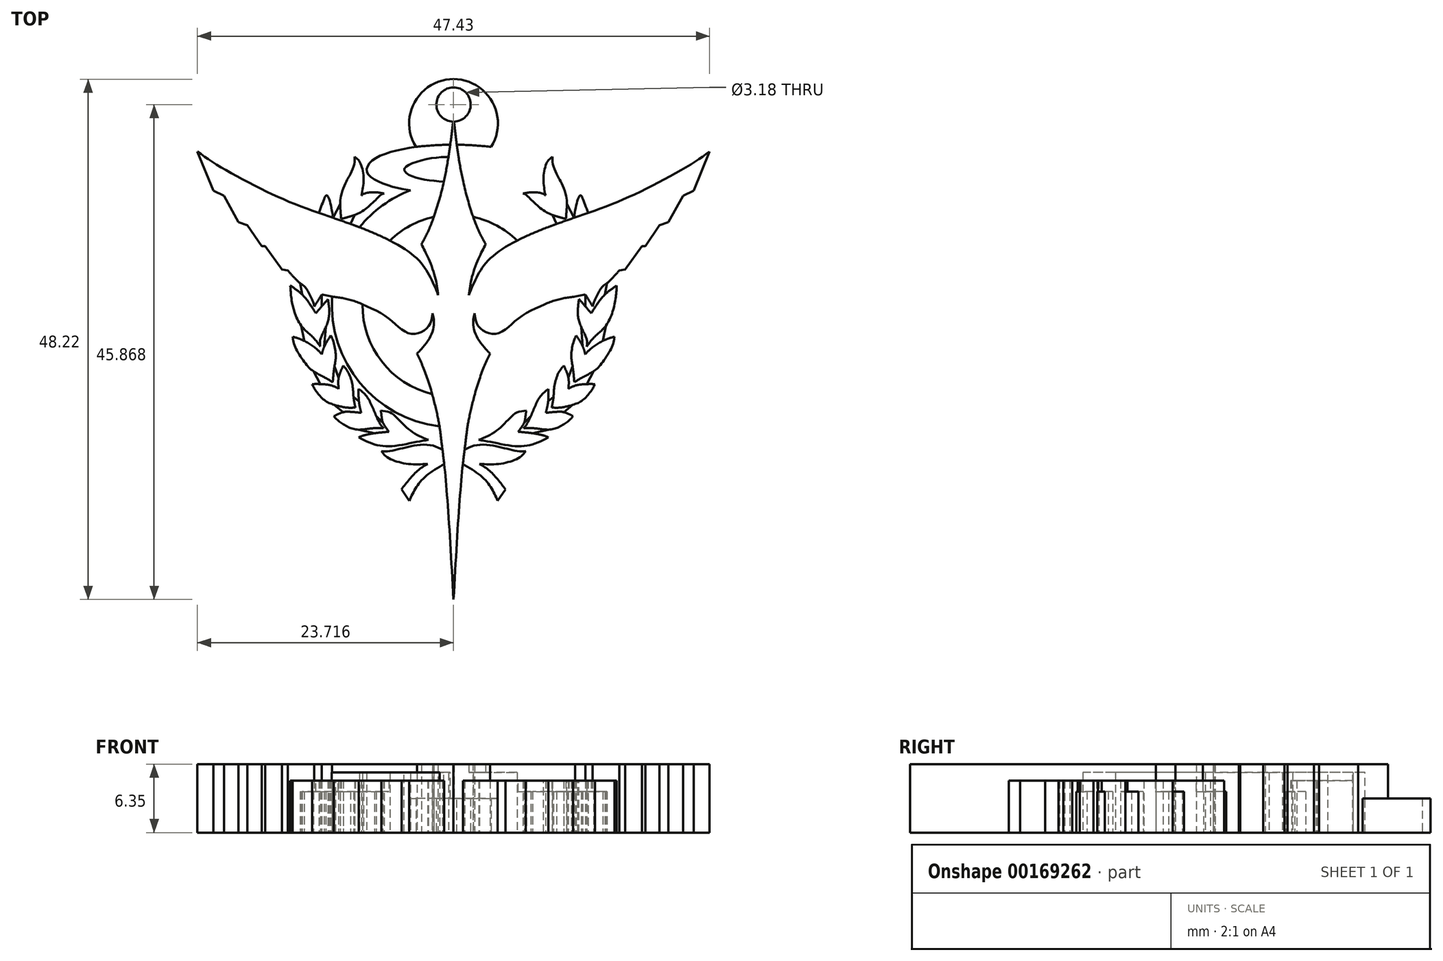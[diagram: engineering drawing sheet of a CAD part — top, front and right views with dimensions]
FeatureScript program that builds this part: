
annotation { "Feature Type Name" : "Feature", "Feature Type Description" : "" }
export const myFeature = defineFeature(function(context is Context, id is Id, definition is map)
    precondition{}
    {
        {
            var Q0;
            Q0=qCreatedBy(makeId("Top.planeOp"),FACE);
            var sketch = newSketch(context, id + "F0", { "sketchPlane" : qUnion([Q0])});
            skFitSpline(sketch, "E0", {"points": [v(-0.2, 21.86) * mm, v(-1.04, 16.18) * mm, v(-2.36, 11.79) * mm, v(-3.17, 10.17) * mm], "startDerivative": vector(-1.64, -14.05) * mm, "endDerivative": vector(-3.45, -6.14) * mm});
            skFitSpline(sketch, "E1", {"points": [v(-3.17, 10.17) * mm, v(-2.63, 9.12) * mm, v(-1.89, 7.1) * mm, v(-1.62, 5.47) * mm], "startDerivative": vector(1.83, -3.3) * mm, "endDerivative": vector(0.52, -4.63) * mm});
            skFitSpline(sketch, "E2", {"points": [v(-1.62, 5.47) * mm, v(-2.4, 7.23) * mm, v(-3.85, 9.08) * mm, v(-8.07, 11.42) * mm, v(-13.34, 13.3) * mm, v(-17.53, 15.06) * mm, v(-21.76, 17.33) * mm, v(-23.91, 18.75) * mm], "startDerivative": vector(-6.88, 17.13) * mm, "endDerivative": vector(-16.15, 11.23) * mm});
            skLineSegment(sketch, "E3", {"start": v(-23.91, 18.75) * mm, "end": v(-22.43, 15.13) * mm});
            skLineSegment(sketch, "E4", {"start": v(-22.43, 15.13) * mm, "end": v(-21.45, 14.66) * mm});
            skLineSegment(sketch, "E5", {"start": v(-21.45, 14.66) * mm, "end": v(-20.1, 12.23) * mm});
            skLineSegment(sketch, "E6", {"start": v(-20.1, 12.23) * mm, "end": v(-19.28, 11.93) * mm});
            skLineSegment(sketch, "E7", {"start": v(-19.28, 11.93) * mm, "end": v(-17.97, 9.98) * mm});
            skLineSegment(sketch, "E8", {"start": v(-17.97, 9.98) * mm, "end": v(-17.65, 9.98) * mm});
            skLineSegment(sketch, "E9", {"start": v(-17.65, 9.98) * mm, "end": v(-16.08, 7.83) * mm});
            skLineSegment(sketch, "E10", {"start": v(-16.08, 7.83) * mm, "end": v(-15.53, 7.73) * mm});
            skFitSpline(sketch, "E11", {"points": [v(-15.53, 7.73) * mm, v(-15.08, 7.22) * mm, v(-14.4, 6.55) * mm, v(-13.97, 6.24) * mm, v(-13.58, 5.63) * mm, v(-13.19, 4.78) * mm, v(-13.09, 4.4) * mm], "startDerivative": vector(2.54, -2.85) * mm, "endDerivative": vector(0.52, -2.73) * mm});
            skFitSpline(sketch, "E12", {"points": [v(-13.09, 4.4) * mm, v(-12.8, 4.88) * mm, v(-12.4, 5.52) * mm], "startDerivative": vector(0.58, 1.01) * mm, "endDerivative": vector(0.8, 1.23) * mm});
            skFitSpline(sketch, "E13", {"points": [v(-12.4, 5.52) * mm, v(-11.44, 5.32) * mm], "startDerivative": vector(0.95, -0.2) * mm, "endDerivative": vector(0.95, -0.2) * mm});
            skArc(sketch, "E14", {"start": v(-4.19, 15.16) * mm, "mid": v(-6.77, 13.76) * mm, "end": v(-8.9, 11.74) * mm});
            skFitSpline(sketch, "E15", {"points": [v(-0.5, 19.4) * mm, v(-3.68, 19.19) * mm, v(-6.74, 18.47) * mm, v(-8.03, 17.61) * mm, v(-8.22, 16.9) * mm, v(-7.62, 16.23) * mm, v(-5.78, 15.49) * mm, v(-4.19, 15.16) * mm], "startDerivative": vector(-16.33, -0.58) * mm, "endDerivative": vector(11.13, -1.82) * mm});
            skFitSpline(sketch, "E16", {"points": [v(-0.66, 18.27) * mm, v(-0.92, 18.25) * mm, v(-2.56, 18.09) * mm, v(-4.33, 17.52) * mm, v(-4.77, 17.11) * mm, v(-4.38, 16.63) * mm, v(-2.99, 16.18) * mm, v(-1.1, 15.96) * mm], "startDerivative": vector(-3.86, -1.21) * mm, "endDerivative": vector(10.06, -0.87) * mm});
            skArc(sketch, "E17.trimOffspring", {"start": v(-11.44, 5.32) * mm, "mid": v(-8.86, -2.68) * mm, "end": v(-1.5, -6.72) * mm});
            skFitSpline(sketch, "E18", {"points": [v(-11.44, 5.32) * mm, v(-9.96, 5.07) * mm, v(-8.12, 4.38) * mm, v(-6.21, 3.3) * mm, v(-4.97, 2.25) * mm, v(-3.92, 1.85) * mm, v(-3.01, 2.13) * mm, v(-2.37, 2.78) * mm, v(-2.15, 3.78) * mm], "startDerivative": vector(11.12, -1.28) * mm, "endDerivative": vector(0.96, 9.95) * mm});
            skFitSpline(sketch, "E19", {"points": [v(-2.15, 3.78) * mm, v(-2.01, 3) * mm, v(-2.39, 1.5) * mm, v(-3.4, 0.2) * mm, v(-3.57, 0.03) * mm], "startDerivative": vector(0.85, -3.16) * mm, "endDerivative": vector(-0.96, -1.05) * mm});
            skFitSpline(sketch, "E20", {"points": [v(-3.57, 0.03) * mm, v(-3.03, -1.16) * mm, v(-2.36, -3.05) * mm, v(-1.77, -5.3) * mm, v(-1.5, -6.72) * mm, v(-1.32, -8.08) * mm, v(-1.09, -9.94) * mm, v(-0.73, -14) * mm, v(-0.2, -22.75) * mm], "startDerivative": vector(5.95, -12.65) * mm, "endDerivative": vector(2.3, -40.95) * mm});
            skArc(sketch, "E21", {"start": v(-2.01, 12.71) * mm, "mid": v(-4.2, 11.9) * mm, "end": v(-6.08, 10.51) * mm});
            skArc(sketch, "E22.trimOffspring", {"start": v(-8.62, 4.6) * mm, "mid": v(-6.85, -0.69) * mm, "end": v(-2.17, -3.71) * mm});
            skFitSpline(sketch, "E23", {"points": [v(-9.37, 18.29) * mm, v(-9.4, 17.58) * mm, v(-9.87, 16.43) * mm, v(-10.1, 16.05) * mm, v(-10.6, 14.72) * mm, v(-10.7, 13.9) * mm, v(-10.6, 12.52) * mm], "startDerivative": vector(0.36, -4.44) * mm, "endDerivative": vector(0.6, -7.53) * mm});
            skFitSpline(sketch, "E24", {"points": [v(-10.6, 12.52) * mm, v(-9.35, 12.88) * mm, v(-8.4, 13.4) * mm, v(-7.35, 14.33) * mm, v(-6.81, 14.81) * mm, v(-6.63, 14.87) * mm], "startDerivative": vector(5.33, 1.36) * mm, "endDerivative": vector(1.78, 0.34) * mm});
            skFitSpline(sketch, "E25", {"points": [v(-6.63, 14.87) * mm, v(-7.46, 15) * mm, v(-8.44, 14.87) * mm, v(-8.7, 14.7) * mm], "startDerivative": vector(-2.08, 0.45) * mm, "endDerivative": vector(-0.93, -0.78) * mm});
            skFitSpline(sketch, "E26", {"points": [v(-8.7, 14.7) * mm, v(-8.53, 16.35) * mm, v(-8.89, 17.8) * mm, v(-9.37, 18.29) * mm], "startDerivative": vector(0.8, 4.17) * mm, "endDerivative": vector(-2.07, 1.52) * mm});
            skFitSpline(sketch, "E27", {"points": [v(-12.66, 13.07) * mm, v(-12.2, 14.33) * mm, v(-11.96, 14.7) * mm, v(-11.7, 14.33) * mm, v(-11.35, 12.62) * mm], "startDerivative": vector(1.61, 4.49) * mm, "endDerivative": vector(0.87, -5.57) * mm});
            skFitSpline(sketch, "E28", {"points": [v(-15.3, 6.34) * mm, v(-15.13, 4.67) * mm, v(-14.31, 2.64) * mm, v(-13.27, 1.61) * mm, v(-12.54, 0.7) * mm], "startDerivative": vector(0.31, -6.23) * mm, "endDerivative": vector(3.16, -4.45) * mm});
            skFitSpline(sketch, "E29", {"points": [v(-12.54, 0.7) * mm, v(-12.54, 1.33) * mm, v(-12.02, 2.49) * mm, v(-11.7, 3.7) * mm, v(-11.81, 5.08) * mm], "startDerivative": vector(-0.45, 3.14) * mm, "endDerivative": vector(-0.71, 5.07) * mm});
            skFitSpline(sketch, "E30", {"points": [v(-11.81, 5.08) * mm, v(-12.4, 4.43) * mm, v(-12.94, 3.77) * mm], "startDerivative": vector(-1.16, -1.28) * mm, "endDerivative": vector(-1.1, -1.33) * mm});
            skFitSpline(sketch, "E31", {"points": [v(-12.94, 3.77) * mm, v(-13.42, 4.52) * mm, v(-14.22, 5.52) * mm, v(-15.3, 6.34) * mm], "startDerivative": vector(-1.54, 2.48) * mm, "endDerivative": vector(-3.16, 2.11) * mm});
            skFitSpline(sketch, "E32", {"points": [v(-15.1, 1.6) * mm, v(-14.03, 1.22) * mm, v(-12.73, 0.33) * mm, v(-12.4, -0.03) * mm], "startDerivative": vector(2.86, -0.78) * mm, "endDerivative": vector(1.1, -1.39) * mm});
            skFitSpline(sketch, "E33", {"points": [v(-12.4, -0.03) * mm, v(-12.16, 0.7) * mm, v(-11.56, 1.72) * mm], "startDerivative": vector(0.38, 1.58) * mm, "endDerivative": vector(1.24, 1.9) * mm});
            skFitSpline(sketch, "E34", {"points": [v(-11.56, 1.72) * mm, v(-11.3, 1.1) * mm, v(-11.1, -0.23) * mm, v(-11.22, -1.13) * mm, v(-11.38, -2.62) * mm], "startDerivative": vector(1.38, -2.72) * mm, "endDerivative": vector(-0.47, -5.48) * mm});
            skFitSpline(sketch, "E35", {"points": [v(-11.38, -2.62) * mm, v(-12, -2.24) * mm, v(-13.17, -1.6) * mm, v(-13.9, -0.9) * mm, v(-14.88, 0.7) * mm, v(-15.1, 1.6) * mm], "startDerivative": vector(-3.43, 2.26) * mm, "endDerivative": vector(-0.6, 4.58) * mm});
            skFitSpline(sketch, "E36", {"points": [v(-10.4, -1.09) * mm, v(-9.92, -1.74) * mm, v(-9.54, -2.96) * mm, v(-9.45, -3.98) * mm, v(-9.28, -4.96) * mm], "startDerivative": vector(2.28, -2.57) * mm, "endDerivative": vector(0.84, -4) * mm});
            skFitSpline(sketch, "E37", {"points": [v(-9.28, -4.96) * mm, v(-10.07, -4.96) * mm, v(-11.24, -4.7) * mm, v(-12.12, -4.3) * mm, v(-12.9, -3.46) * mm, v(-13.29, -2.8) * mm], "startDerivative": vector(-4.07, -0.25) * mm, "endDerivative": vector(-1.83, 3.6) * mm});
            skFitSpline(sketch, "E38", {"points": [v(-13.29, -2.8) * mm, v(-12.54, -2.8) * mm, v(-11.49, -2.92) * mm, v(-10.83, -3.23) * mm], "startDerivative": vector(2.24, 0.04) * mm, "endDerivative": vector(1.91, -1.15) * mm});
            skFitSpline(sketch, "E39", {"points": [v(-10.83, -3.23) * mm, v(-10.83, -2.2) * mm, v(-10.4, -1.09) * mm], "startDerivative": vector(-0.2, 2.12) * mm, "endDerivative": vector(1.03, 2.17) * mm});
            skFitSpline(sketch, "E40", {"points": [v(-8.99, -3.23) * mm, v(-8.96, -4.4) * mm, v(-8.74, -5.45) * mm], "startDerivative": vector(-0.04, -2.32) * mm, "endDerivative": vector(0.53, -2.11) * mm});
            skFitSpline(sketch, "E41", {"points": [v(-8.99, -3.23) * mm, v(-8.3, -3.84) * mm, v(-7.8, -4.72) * mm, v(-7.35, -5.76) * mm, v(-7, -6.47) * mm, v(-6.7, -6.88) * mm], "startDerivative": vector(3.52, -2.72) * mm, "endDerivative": vector(1.96, -2.49) * mm});
            skFitSpline(sketch, "E42", {"points": [v(-6.7, -6.88) * mm, v(-7.68, -6.88) * mm, v(-8.99, -7) * mm, v(-9.98, -6.75) * mm, v(-10.83, -6.21) * mm, v(-11.27, -5.76) * mm], "startDerivative": vector(-4.66, 0.24) * mm, "endDerivative": vector(-2.42, 2.81) * mm});
            skFitSpline(sketch, "E43", {"points": [v(-11.27, -5.76) * mm, v(-10.4, -5.4) * mm, v(-9.7, -5.36) * mm, v(-8.74, -5.45) * mm], "startDerivative": vector(2.56, 1.31) * mm, "endDerivative": vector(2.83, -0.28) * mm});
            skFitSpline(sketch, "E44", {"points": [v(-6.94, -5.25) * mm, v(-6.03, -5.45) * mm, v(-5.3, -6.06) * mm, v(-4.45, -6.88) * mm, v(-3.49, -7.55) * mm, v(-2.54, -7.95) * mm], "startDerivative": vector(5.08, -0.54) * mm, "endDerivative": vector(4.83, -1.76) * mm});
            skFitSpline(sketch, "E45", {"points": [v(-2.54, -7.95) * mm, v(-3.74, -8.17) * mm, v(-5.55, -8.5) * mm, v(-6.84, -8.52) * mm, v(-7.9, -8.25) * mm, v(-8.99, -7.72) * mm], "startDerivative": vector(-5.85, -1.06) * mm, "endDerivative": vector(-5.7, 3) * mm});
            skFitSpline(sketch, "E46", {"points": [v(-8.99, -7.72) * mm, v(-8.33, -7.5) * mm, v(-6.85, -7.27) * mm, v(-6.19, -7.2) * mm], "startDerivative": vector(1.91, 0.82) * mm, "endDerivative": vector(2.02, 0.14) * mm});
            skFitSpline(sketch, "E47", {"points": [v(-6.19, -7.2) * mm, v(-6.74, -6.34) * mm, v(-6.94, -5.25) * mm], "startDerivative": vector(-0.92, 1.48) * mm, "endDerivative": vector(-0.6, 2.4) * mm});
            skFitSpline(sketch, "E48", {"points": [v(-1.21, -8.9) * mm, v(-2.02, -8.52) * mm, v(-3.33, -8.42) * mm, v(-4.58, -8.65) * mm, v(-5.49, -8.86) * mm, v(-6.36, -9.03) * mm, v(-6.87, -8.99) * mm], "startDerivative": vector(-4.57, 2.68) * mm, "endDerivative": vector(-3.88, 0.62) * mm});
            skFitSpline(sketch, "E49", {"points": [v(-6.87, -8.99) * mm, v(-6.38, -9.54) * mm, v(-5.41, -9.98) * mm, v(-4.03, -10.22) * mm, v(-2.59, -10.18) * mm], "startDerivative": vector(2.13, -2.92) * mm, "endDerivative": vector(5.13, 0.36) * mm});
            skFitSpline(sketch, "E50", {"points": [v(-2.59, -10.18) * mm, v(-3.48, -10.77) * mm, v(-4.3, -11.64) * mm, v(-5.01, -12.54) * mm], "startDerivative": vector(-2.84, -1.64) * mm, "endDerivative": vector(-2.12, -2.64) * mm});
            skLineSegment(sketch, "E51", {"start": v(-5.01, -12.54) * mm, "end": v(-4.3, -13.6) * mm});
            skFitSpline(sketch, "E52", {"points": [v(-4.3, -13.6) * mm, v(-3.76, -12.56) * mm, v(-2.85, -11.4) * mm, v(-1.06, -10.2) * mm], "startDerivative": vector(1.7, 3.6) * mm, "endDerivative": vector(4.97, 2.9) * mm});
            skLineSegment(sketch, "E53", {"start": v(-10.7, 13.9) * mm, "end": v(-11.35, 12.62) * mm});
            skLineSegment(sketch, "E54", {"start": v(-9.35, 12.88) * mm, "end": v(-9.73, 12.05) * mm});
            skLineSegment(sketch, "E55", {"start": v(-13.17, -1.6) * mm, "end": v(-12.54, -2.8) * mm});
            skLineSegment(sketch, "E56", {"start": v(-11.22, -1.13) * mm, "end": v(-10.83, -2.2) * mm});
            skLineSegment(sketch, "E57", {"start": v(-11.24, -4.7) * mm, "end": v(-10.4, -5.4) * mm});
            skLineSegment(sketch, "E58", {"start": v(-9.45, -3.98) * mm, "end": v(-8.96, -4.4) * mm});
            skLineSegment(sketch, "E59", {"start": v(-8.99, -7) * mm, "end": v(-7.5, -7.34) * mm});
            skLineSegment(sketch, "E60", {"start": v(-7.35, -5.76) * mm, "end": v(-6.74, -6.34) * mm});
            skFitSpline(sketch, "E61.MirrorCS", {"points": [v(-0.2, 21.86) * mm, v(0.66, 16.18) * mm, v(1.97, 11.79) * mm, v(2.79, 10.17) * mm], "startDerivative": vector(1.64, -14.05) * mm, "endDerivative": vector(3.45, -6.14) * mm});
            skFitSpline(sketch, "E62.MirrorCS", {"points": [v(2.79, 10.17) * mm, v(2.24, 9.12) * mm, v(1.5, 7.1) * mm, v(1.23, 5.47) * mm], "startDerivative": vector(-1.83, -3.3) * mm, "endDerivative": vector(-0.52, -4.63) * mm});
            skFitSpline(sketch, "E63.MirrorCS", {"points": [v(1.23, 5.47) * mm, v(2, 7.23) * mm, v(3.46, 9.08) * mm, v(7.68, 11.42) * mm, v(12.96, 13.3) * mm, v(17.15, 15.06) * mm, v(21.37, 17.33) * mm, v(23.52, 18.75) * mm], "startDerivative": vector(6.88, 17.13) * mm, "endDerivative": vector(16.15, 11.23) * mm});
            skArc(sketch, "E64.MirrorCS", {"start": v(1.62, 12.71) * mm, "mid": v(3.81, 11.9) * mm, "end": v(5.7, 10.51) * mm});
            skArc(sketch, "E65.MirrorCS", {"start": v(3.8, 15.16) * mm, "mid": v(6.38, 13.76) * mm, "end": v(8.52, 11.74) * mm});
            skFitSpline(sketch, "E66.MirrorCS", {"points": [v(0.1, 19.4) * mm, v(3.3, 19.19) * mm, v(6.35, 18.47) * mm, v(7.64, 17.61) * mm, v(7.84, 16.9) * mm, v(7.24, 16.23) * mm, v(5.4, 15.49) * mm, v(3.8, 15.16) * mm], "startDerivative": vector(16.33, -0.58) * mm, "endDerivative": vector(-11.13, -1.82) * mm});
            skFitSpline(sketch, "E67.MirrorCS", {"points": [v(0.27, 18.27) * mm, v(0.53, 18.25) * mm, v(2.17, 18.09) * mm, v(3.94, 17.52) * mm, v(4.38, 17.11) * mm, v(3.99, 16.63) * mm, v(2.6, 16.18) * mm, v(0.7, 15.96) * mm], "startDerivative": vector(3.86, -1.21) * mm, "endDerivative": vector(-10.06, -0.87) * mm});
            skFitSpline(sketch, "E68.MirrorCS", {"points": [v(8.98, 18.29) * mm, v(9.01, 17.58) * mm, v(9.49, 16.43) * mm, v(9.7, 16.05) * mm, v(10.22, 14.72) * mm, v(10.3, 13.9) * mm, v(10.22, 12.52) * mm], "startDerivative": vector(-0.36, -4.44) * mm, "endDerivative": vector(-0.6, -7.53) * mm});
            skFitSpline(sketch, "E69.MirrorCS", {"points": [v(8.32, 14.7) * mm, v(8.14, 16.35) * mm, v(8.5, 17.8) * mm, v(8.98, 18.29) * mm], "startDerivative": vector(-0.8, 4.17) * mm, "endDerivative": vector(2.07, 1.52) * mm});
            skFitSpline(sketch, "E70.MirrorCS", {"points": [v(6.24, 14.87) * mm, v(7.07, 15) * mm, v(8.05, 14.87) * mm, v(8.32, 14.7) * mm], "startDerivative": vector(2.08, 0.45) * mm, "endDerivative": vector(0.93, -0.78) * mm});
            skFitSpline(sketch, "E71.MirrorCS", {"points": [v(10.22, 12.52) * mm, v(8.97, 12.88) * mm, v(8, 13.4) * mm, v(6.97, 14.33) * mm, v(6.42, 14.81) * mm, v(6.24, 14.87) * mm], "startDerivative": vector(-5.33, 1.36) * mm, "endDerivative": vector(-1.78, 0.34) * mm});
            skLineSegment(sketch, "E72.MirrorCS", {"start": v(10.3, 13.9) * mm, "end": v(10.96, 12.62) * mm});
            skLineSegment(sketch, "E73.MirrorCS", {"start": v(8.97, 12.88) * mm, "end": v(9.35, 12.05) * mm});
            skFitSpline(sketch, "E74.MirrorCS", {"points": [v(12.27, 13.07) * mm, v(11.8, 14.33) * mm, v(11.57, 14.7) * mm, v(11.32, 14.33) * mm, v(10.96, 12.62) * mm], "startDerivative": vector(-1.61, 4.49) * mm, "endDerivative": vector(-0.87, -5.57) * mm});
            skFitSpline(sketch, "E75.MirrorCS", {"points": [v(1.23, 5.47) * mm, v(2, 7.23) * mm, v(3.46, 9.08) * mm, v(7.68, 11.42) * mm, v(12.96, 13.3) * mm, v(17.15, 15.06) * mm, v(21.37, 17.33) * mm, v(23.52, 18.75) * mm], "startDerivative": vector(6.88, 17.13) * mm, "endDerivative": vector(16.15, 11.23) * mm});
            skLineSegment(sketch, "E76.MirrorCS", {"start": v(17.26, 9.98) * mm, "end": v(15.7, 7.83) * mm});
            skLineSegment(sketch, "E77.MirrorCS", {"start": v(18.89, 11.93) * mm, "end": v(17.58, 9.98) * mm});
            skLineSegment(sketch, "E78.MirrorCS", {"start": v(17.58, 9.98) * mm, "end": v(17.26, 9.98) * mm});
            skLineSegment(sketch, "E79.MirrorCS", {"start": v(21.07, 14.66) * mm, "end": v(19.71, 12.23) * mm});
            skLineSegment(sketch, "E80.MirrorCS", {"start": v(19.71, 12.23) * mm, "end": v(18.89, 11.93) * mm});
            skLineSegment(sketch, "E81.MirrorCS", {"start": v(22.05, 15.13) * mm, "end": v(21.07, 14.66) * mm});
            skLineSegment(sketch, "E82.MirrorCS", {"start": v(23.52, 18.75) * mm, "end": v(22.05, 15.13) * mm});
            skFitSpline(sketch, "E83.MirrorCS", {"points": [v(15.14, 7.73) * mm, v(14.69, 7.22) * mm, v(14, 6.55) * mm, v(13.58, 6.24) * mm, v(13.2, 5.63) * mm, v(12.8, 4.78) * mm, v(12.7, 4.4) * mm], "startDerivative": vector(-2.54, -2.85) * mm, "endDerivative": vector(-0.52, -2.73) * mm});
            skFitSpline(sketch, "E84.MirrorCS", {"points": [v(12.56, 3.77) * mm, v(13.04, 4.52) * mm, v(13.84, 5.52) * mm, v(14.92, 6.34) * mm], "startDerivative": vector(1.54, 2.48) * mm, "endDerivative": vector(3.16, 2.11) * mm});
            skFitSpline(sketch, "E85.MirrorCS", {"points": [v(12.7, 4.4) * mm, v(12.42, 4.88) * mm, v(12, 5.52) * mm], "startDerivative": vector(-0.58, 1.01) * mm, "endDerivative": vector(-0.8, 1.23) * mm});
            skFitSpline(sketch, "E86.MirrorCS", {"points": [v(11.43, 5.08) * mm, v(12, 4.43) * mm, v(12.56, 3.77) * mm], "startDerivative": vector(1.16, -1.28) * mm, "endDerivative": vector(1.1, -1.33) * mm});
            skFitSpline(sketch, "E87.MirrorCS", {"points": [v(12, 5.52) * mm, v(11.05, 5.32) * mm], "startDerivative": vector(-0.95, -0.2) * mm, "endDerivative": vector(-0.95, -0.2) * mm});
            skArc(sketch, "E88.MirrorCS", {"start": v(11.05, 5.32) * mm, "mid": v(8.47, -2.68) * mm, "end": v(1.1, -6.72) * mm});
            skFitSpline(sketch, "E89.MirrorCS", {"points": [v(11.05, 5.32) * mm, v(9.58, 5.07) * mm, v(7.74, 4.38) * mm, v(5.83, 3.3) * mm, v(4.58, 2.25) * mm, v(3.53, 1.85) * mm, v(2.62, 2.13) * mm, v(1.98, 2.78) * mm, v(1.76, 3.78) * mm], "startDerivative": vector(-11.12, -1.28) * mm, "endDerivative": vector(-0.96, 9.95) * mm});
            skArc(sketch, "E90.MirrorCS", {"start": v(8.23, 4.6) * mm, "mid": v(6.47, -0.69) * mm, "end": v(1.78, -3.71) * mm});
            skFitSpline(sketch, "E91.MirrorCS", {"points": [v(1.76, 3.78) * mm, v(1.63, 3) * mm, v(2, 1.5) * mm, v(3.02, 0.2) * mm, v(3.18, 0.03) * mm], "startDerivative": vector(-0.85, -3.16) * mm, "endDerivative": vector(0.96, -1.05) * mm});
            skFitSpline(sketch, "E92.MirrorCS", {"points": [v(3.18, 0.03) * mm, v(2.65, -1.16) * mm, v(1.98, -3.05) * mm, v(1.39, -5.3) * mm, v(1.1, -6.72) * mm, v(0.93, -8.08) * mm, v(0.7, -9.94) * mm, v(0.34, -14) * mm, v(-0.2, -22.75) * mm], "startDerivative": vector(-5.95, -12.65) * mm, "endDerivative": vector(-2.3, -40.95) * mm});
            skLineSegment(sketch, "E93.MirrorCS", {"start": v(15.7, 7.83) * mm, "end": v(15.14, 7.73) * mm});
            skFitSpline(sketch, "E94.MirrorCS", {"points": [v(14.92, 6.34) * mm, v(14.74, 4.67) * mm, v(13.93, 2.64) * mm, v(12.89, 1.61) * mm, v(12.15, 0.7) * mm], "startDerivative": vector(-0.31, -6.23) * mm, "endDerivative": vector(-3.16, -4.45) * mm});
            skFitSpline(sketch, "E95.MirrorCS", {"points": [v(12.15, 0.7) * mm, v(12.15, 1.33) * mm, v(11.64, 2.49) * mm, v(11.32, 3.7) * mm, v(11.43, 5.08) * mm], "startDerivative": vector(0.45, 3.14) * mm, "endDerivative": vector(0.71, 5.07) * mm});
            skFitSpline(sketch, "E96.MirrorCS", {"points": [v(12.56, 3.77) * mm, v(13.04, 4.52) * mm, v(13.84, 5.52) * mm, v(14.92, 6.34) * mm], "startDerivative": vector(1.54, 2.48) * mm, "endDerivative": vector(3.16, 2.11) * mm});
            skFitSpline(sketch, "E97.MirrorCS", {"points": [v(12.15, 0.7) * mm, v(12.15, 1.33) * mm, v(11.64, 2.49) * mm, v(11.32, 3.7) * mm, v(11.43, 5.08) * mm], "startDerivative": vector(0.45, 3.14) * mm, "endDerivative": vector(0.71, 5.07) * mm});
            skFitSpline(sketch, "E98.MirrorCS", {"points": [v(14.92, 6.34) * mm, v(14.74, 4.67) * mm, v(13.93, 2.64) * mm, v(12.89, 1.61) * mm, v(12.15, 0.7) * mm], "startDerivative": vector(-0.31, -6.23) * mm, "endDerivative": vector(-3.16, -4.45) * mm});
            skFitSpline(sketch, "E99.MirrorCS", {"points": [v(12, -0.03) * mm, v(11.78, 0.7) * mm, v(11.17, 1.72) * mm], "startDerivative": vector(-0.38, 1.58) * mm, "endDerivative": vector(-1.24, 1.9) * mm});
            skFitSpline(sketch, "E100.MirrorCS", {"points": [v(14.71, 1.6) * mm, v(13.65, 1.22) * mm, v(12.34, 0.33) * mm, v(12, -0.03) * mm], "startDerivative": vector(-2.86, -0.78) * mm, "endDerivative": vector(-1.1, -1.39) * mm});
            skFitSpline(sketch, "E101.MirrorCS", {"points": [v(11, -2.62) * mm, v(11.62, -2.24) * mm, v(12.78, -1.6) * mm, v(13.5, -0.9) * mm, v(14.49, 0.7) * mm, v(14.71, 1.6) * mm], "startDerivative": vector(3.43, 2.26) * mm, "endDerivative": vector(0.6, 4.58) * mm});
            skFitSpline(sketch, "E102.MirrorCS", {"points": [v(11.17, 1.72) * mm, v(10.91, 1.1) * mm, v(10.71, -0.23) * mm, v(10.83, -1.13) * mm, v(11, -2.62) * mm], "startDerivative": vector(-1.38, -2.72) * mm, "endDerivative": vector(0.47, -5.48) * mm});
            skLineSegment(sketch, "E103.MirrorCS", {"start": v(12.78, -1.6) * mm, "end": v(12.15, -2.8) * mm});
            skLineSegment(sketch, "E104.MirrorCS", {"start": v(10.83, -1.13) * mm, "end": v(10.45, -2.2) * mm});
            skFitSpline(sketch, "E105.MirrorCS", {"points": [v(10.45, -3.23) * mm, v(10.45, -2.2) * mm, v(10.02, -1.09) * mm], "startDerivative": vector(0.2, 2.12) * mm, "endDerivative": vector(-1.03, 2.17) * mm});
            skFitSpline(sketch, "E106.MirrorCS", {"points": [v(12.9, -2.8) * mm, v(12.15, -2.8) * mm, v(11.1, -2.92) * mm, v(10.45, -3.23) * mm], "startDerivative": vector(-2.24, 0.04) * mm, "endDerivative": vector(-1.91, -1.15) * mm});
            skFitSpline(sketch, "E107.MirrorCS", {"points": [v(8.9, -4.96) * mm, v(9.68, -4.96) * mm, v(10.86, -4.7) * mm, v(11.74, -4.3) * mm, v(12.52, -3.46) * mm, v(12.9, -2.8) * mm], "startDerivative": vector(4.07, -0.25) * mm, "endDerivative": vector(1.83, 3.6) * mm});
            skFitSpline(sketch, "E108.MirrorCS", {"points": [v(10.02, -1.09) * mm, v(9.54, -1.74) * mm, v(9.15, -2.96) * mm, v(9.07, -3.98) * mm, v(8.9, -4.96) * mm], "startDerivative": vector(-2.28, -2.57) * mm, "endDerivative": vector(-0.84, -4) * mm});
            skLineSegment(sketch, "E109.MirrorCS", {"start": v(10.86, -4.7) * mm, "end": v(10.02, -5.4) * mm});
            skLineSegment(sketch, "E110.MirrorCS", {"start": v(9.07, -3.98) * mm, "end": v(8.57, -4.4) * mm});
            skFitSpline(sketch, "E111.MirrorCS", {"points": [v(8.6, -3.23) * mm, v(8.57, -4.4) * mm, v(8.36, -5.45) * mm], "startDerivative": vector(0.04, -2.32) * mm, "endDerivative": vector(-0.53, -2.11) * mm});
            skFitSpline(sketch, "E112.MirrorCS", {"points": [v(10.89, -5.76) * mm, v(10.02, -5.4) * mm, v(9.3, -5.36) * mm, v(8.36, -5.45) * mm], "startDerivative": vector(-2.56, 1.31) * mm, "endDerivative": vector(-2.83, -0.28) * mm});
            skFitSpline(sketch, "E113.MirrorCS", {"points": [v(6.31, -6.88) * mm, v(7.3, -6.88) * mm, v(8.6, -7) * mm, v(9.6, -6.75) * mm, v(10.45, -6.21) * mm, v(10.89, -5.76) * mm], "startDerivative": vector(4.66, 0.24) * mm, "endDerivative": vector(2.42, 2.81) * mm});
            skFitSpline(sketch, "E114.MirrorCS", {"points": [v(8.6, -3.23) * mm, v(7.92, -3.84) * mm, v(7.4, -4.72) * mm, v(6.96, -5.76) * mm, v(6.6, -6.47) * mm, v(6.31, -6.88) * mm], "startDerivative": vector(-3.52, -2.72) * mm, "endDerivative": vector(-1.96, -2.49) * mm});
            skLineSegment(sketch, "E115.MirrorCS", {"start": v(6.96, -5.76) * mm, "end": v(6.35, -6.34) * mm});
            skLineSegment(sketch, "E116.MirrorCS", {"start": v(8.6, -7) * mm, "end": v(7.12, -7.34) * mm});
            skFitSpline(sketch, "E117.MirrorCS", {"points": [v(8.6, -7.72) * mm, v(7.94, -7.5) * mm, v(6.47, -7.27) * mm, v(5.8, -7.2) * mm], "startDerivative": vector(-1.91, 0.82) * mm, "endDerivative": vector(-2.02, 0.14) * mm});
            skFitSpline(sketch, "E118.MirrorCS", {"points": [v(5.8, -7.2) * mm, v(6.35, -6.34) * mm, v(6.55, -5.25) * mm], "startDerivative": vector(0.92, 1.48) * mm, "endDerivative": vector(0.6, 2.4) * mm});
            skFitSpline(sketch, "E119.MirrorCS", {"points": [v(6.55, -5.25) * mm, v(5.64, -5.45) * mm, v(4.9, -6.06) * mm, v(4.07, -6.88) * mm, v(3.1, -7.55) * mm, v(2.15, -7.95) * mm], "startDerivative": vector(-5.08, -0.54) * mm, "endDerivative": vector(-4.83, -1.76) * mm});
            skFitSpline(sketch, "E120.MirrorCS", {"points": [v(2.15, -7.95) * mm, v(3.36, -8.17) * mm, v(5.16, -8.5) * mm, v(6.45, -8.52) * mm, v(7.5, -8.25) * mm, v(8.6, -7.72) * mm], "startDerivative": vector(5.85, -1.06) * mm, "endDerivative": vector(5.7, 3) * mm});
            skFitSpline(sketch, "E121.MirrorCS", {"points": [v(0.83, -8.9) * mm, v(1.63, -8.52) * mm, v(2.94, -8.42) * mm, v(4.19, -8.65) * mm, v(5.1, -8.86) * mm, v(5.97, -9.03) * mm, v(6.48, -8.99) * mm], "startDerivative": vector(4.57, 2.68) * mm, "endDerivative": vector(3.88, 0.62) * mm});
            skFitSpline(sketch, "E122.MirrorCS", {"points": [v(6.48, -8.99) * mm, v(6, -9.54) * mm, v(5.02, -9.98) * mm, v(3.64, -10.22) * mm, v(2.2, -10.18) * mm], "startDerivative": vector(-2.13, -2.92) * mm, "endDerivative": vector(-5.13, 0.36) * mm});
            skFitSpline(sketch, "E123.MirrorCS", {"points": [v(2.2, -10.18) * mm, v(3.1, -10.77) * mm, v(3.9, -11.64) * mm, v(4.63, -12.54) * mm], "startDerivative": vector(2.84, -1.64) * mm, "endDerivative": vector(2.12, -2.64) * mm});
            skFitSpline(sketch, "E124.MirrorCS", {"points": [v(3.9, -13.6) * mm, v(3.37, -12.56) * mm, v(2.46, -11.4) * mm, v(0.67, -10.2) * mm], "startDerivative": vector(-1.7, 3.6) * mm, "endDerivative": vector(-4.97, 2.9) * mm});
            skLineSegment(sketch, "E125.MirrorCS", {"start": v(4.63, -12.54) * mm, "end": v(3.9, -13.6) * mm});
            skCircle(sketch, "E126", {"center": v(-0.2, 23.12) * mm, "radius": 1.59 * mm});
            skArc(sketch, "E127", {"start": v(3.3, 19.19) * mm, "mid": v(-0.2, 25.47) * mm, "end": v(-3.68, 19.19) * mm});
            skLineSegment(sketch, "E128", {"start": v(-14.4, 6.55) * mm, "end": v(-14.22, 5.52) * mm});
            skLineSegment(sketch, "E129", {"start": v(-12.4, 5.52) * mm, "end": v(-12.4, 4.43) * mm});
            skLineSegment(sketch, "E130", {"start": v(-14.31, 2.64) * mm, "end": v(-14.03, 1.22) * mm});
            skLineSegment(sketch, "E131", {"start": v(-12.02, 2.49) * mm, "end": v(-12.16, 0.7) * mm});
            skLineSegment(sketch, "E132.MirrorCS", {"start": v(14, 6.55) * mm, "end": v(13.84, 5.52) * mm});
            skLineSegment(sketch, "E133.MirrorCS", {"start": v(12, 5.52) * mm, "end": v(12, 4.43) * mm});
            skLineSegment(sketch, "E134.MirrorCS", {"start": v(13.93, 2.64) * mm, "end": v(13.65, 1.22) * mm});
            skLineSegment(sketch, "E135.MirrorCS", {"start": v(11.64, 2.49) * mm, "end": v(11.78, 0.7) * mm});
            skSolve(sketch);
        }
        {
            var Q0;
            {var subQ33=sQuery(id+"F0.wireOp",EDGE,"E1");Q0=makeQuery(id+"F0.imprint","IMPRINT",FACE,{"disambiguationData":[TD([[makeQuery(id+"F0.imprint","IMPRINT",EDGE,{"derivedFrom":subQ33}),1.0]])]});}
            extrude(context, id + "F1", {"entities" : qUnion([Q0]), "depth" : 6.35 * mm});
        }
        {
            var Q0;
            {var subQ1=sQuery(id+"F0.wireOp",EDGE,"E64.MirrorCS");Q0=makeQuery(id+"F0.imprint","IMPRINT",FACE,{"disambiguationData":[TD([[makeQuery(id+"F0.imprint","IMPRINT",EDGE,{"derivedFrom":subQ1}),1.0]])]});}
            var Q1;
            {var subQ0=sQuery(id+"F0.wireOp",EDGE,"E14");Q1=makeQuery(id+"F0.imprint","IMPRINT",FACE,{"disambiguationData":[TD([[makeQuery(id+"F0.imprint","IMPRINT",EDGE,{"derivedFrom":subQ0}),1.0]])]});}
            var Q2;
            {var subQ0=sQuery(id+"F0.wireOp",EDGE,"E17.trimOffspring");Q2=makeQuery(id+"F0.imprint","IMPRINT",FACE,{"disambiguationData":[TD([[makeQuery(id+"F0.imprint","IMPRINT",EDGE,{"derivedFrom":subQ0}),1.0]])]});}
            var Q3;
            {var subQ0=sQuery(id+"F0.wireOp",EDGE,"E88.MirrorCS");Q3=makeQuery(id+"F0.imprint","IMPRINT",FACE,{"disambiguationData":[TD([[makeQuery(id+"F0.imprint","IMPRINT",EDGE,{"derivedFrom":subQ0}),-1.0]])]});}
            extrude(context, id + "F2", {"entities" : qUnion([Q0, Q1, Q2, Q3]), "operationType" : NewBodyOperationType.ADD, "depth" : 5.6 * mm});
        }
        {
            var Q0;
            {var subQ1=sQuery(id+"F0.wireOp",EDGE,"E69.MirrorCS");Q0=makeQuery(id+"F0.imprint","IMPRINT",FACE,{"disambiguationData":[TD([[makeQuery(id+"F0.imprint","IMPRINT",EDGE,{"derivedFrom":subQ1}),-1.0]])]});}
            var Q1;
            {var subQ0=sQuery(id+"F0.wireOp",EDGE,"E74.MirrorCS");Q1=makeQuery(id+"F0.imprint","IMPRINT",FACE,{"disambiguationData":[TD([[makeQuery(id+"F0.imprint","IMPRINT",EDGE,{"derivedFrom":subQ0}),1.0]])]});}
            var Q2;
            {var subQ8=sQuery(id+"F0.wireOp",EDGE,"E86.MirrorCS");Q2=makeQuery(id+"F0.imprint","IMPRINT",FACE,{"disambiguationData":[TD([[makeQuery(id+"F0.imprint","IMPRINT",EDGE,{"derivedFrom":subQ8}),-1.0]])]});}
            var Q3;
            {var subQ6=sQuery(id+"F0.wireOp",EDGE,"E99.MirrorCS");Q3=makeQuery(id+"F0.imprint","IMPRINT",FACE,{"disambiguationData":[TD([[makeQuery(id+"F0.imprint","IMPRINT",EDGE,{"derivedFrom":subQ6}),1.0]])]});}
            var Q4;
            {var subQ2=sQuery(id+"F0.wireOp",EDGE,"E105.MirrorCS");var subQ6=makeQuery(id+"F0.imprint","INTERSECT",VERTEX,{"derivedFrom":[sQuery(id+"F0.wireOp",EDGE,"E104.MirrorCS"),subQ2]});Q4=makeQuery(id+"F0.imprint","IMPRINT",FACE,{"disambiguationData":[TD([[makeQuery(id+"F0.imprint","IMPRINT",EDGE,{"disambiguationData":[TD([[subQ6,1.0]])],"derivedFrom":subQ2}),1.0]])]});}
            var Q5;
            {var subQ2=sQuery(id+"F0.wireOp",EDGE,"E111.MirrorCS");var subQ6=makeQuery(id+"F0.imprint","INTERSECT",VERTEX,{"derivedFrom":[sQuery(id+"F0.wireOp",EDGE,"E110.MirrorCS"),subQ2]});Q5=makeQuery(id+"F0.imprint","IMPRINT",FACE,{"disambiguationData":[TD([[makeQuery(id+"F0.imprint","IMPRINT",EDGE,{"disambiguationData":[TD([[subQ6,1.0]])],"derivedFrom":subQ2}),-1.0]])]});}
            var Q6;
            {var subQ2=sQuery(id+"F0.wireOp",EDGE,"E119.MirrorCS");Q6=makeQuery(id+"F0.imprint","IMPRINT",FACE,{"disambiguationData":[TD([[makeQuery(id+"F0.imprint","IMPRINT",EDGE,{"derivedFrom":subQ2}),1.0]])]});}
            var Q7;
            {var subQ2=sQuery(id+"F0.wireOp",EDGE,"E122.MirrorCS");Q7=makeQuery(id+"F0.imprint","IMPRINT",FACE,{"disambiguationData":[TD([[makeQuery(id+"F0.imprint","IMPRINT",EDGE,{"derivedFrom":subQ2}),-1.0]])]});}
            var Q8;
            {var subQ0=sQuery(id+"F0.wireOp",EDGE,"E49");Q8=makeQuery(id+"F0.imprint","IMPRINT",FACE,{"disambiguationData":[TD([[makeQuery(id+"F0.imprint","IMPRINT",EDGE,{"derivedFrom":subQ0}),1.0]])]});}
            var Q9;
            {var subQ5=sQuery(id+"F0.wireOp",EDGE,"E44");Q9=makeQuery(id+"F0.imprint","IMPRINT",FACE,{"disambiguationData":[TD([[makeQuery(id+"F0.imprint","IMPRINT",EDGE,{"derivedFrom":subQ5}),-1.0]])]});}
            var Q10;
            {var subQ1=sQuery(id+"F0.wireOp",EDGE,"E41");var subQ4=sQuery(id+"F0.wireOp",EDGE,"E40");var subQ5=makeQuery(id+"F0.imprint","INTERSECT",VERTEX,{"derivedFrom":[subQ4,subQ1]});Q10=makeQuery(id+"F0.imprint","IMPRINT",FACE,{"disambiguationData":[TD([[makeQuery(id+"F0.imprint","IMPRINT",EDGE,{"disambiguationData":[TD([[subQ5,-1.0]])],"derivedFrom":subQ4}),1.0]])]});}
            var Q11;
            {var subQ4=sQuery(id+"F0.wireOp",EDGE,"E36");var subQ7=sQuery(id+"F0.wireOp",EDGE,"E39");var subQ8=makeQuery(id+"F0.imprint","INTERSECT",VERTEX,{"derivedFrom":[subQ4,subQ7]});Q11=makeQuery(id+"F0.imprint","IMPRINT",FACE,{"disambiguationData":[TD([[makeQuery(id+"F0.imprint","IMPRINT",EDGE,{"disambiguationData":[TD([[subQ8,-1.0]])],"derivedFrom":subQ4}),-1.0]])]});}
            var Q12;
            {var subQ1=sQuery(id+"F0.wireOp",EDGE,"E33");Q12=makeQuery(id+"F0.imprint","IMPRINT",FACE,{"disambiguationData":[TD([[makeQuery(id+"F0.imprint","IMPRINT",EDGE,{"derivedFrom":subQ1}),-1.0]])]});}
            var Q13;
            {var subQ0=sQuery(id+"F0.wireOp",EDGE,"E30");Q13=makeQuery(id+"F0.imprint","IMPRINT",FACE,{"disambiguationData":[TD([[makeQuery(id+"F0.imprint","IMPRINT",EDGE,{"derivedFrom":subQ0}),1.0]])]});}
            var Q14;
            {var subQ0=sQuery(id+"F0.wireOp",EDGE,"E25");Q14=makeQuery(id+"F0.imprint","IMPRINT",FACE,{"disambiguationData":[TD([[makeQuery(id+"F0.imprint","IMPRINT",EDGE,{"derivedFrom":subQ0}),1.0]])]});}
            var Q15;
            {var subQ0=sQuery(id+"F0.wireOp",EDGE,"E27");Q15=makeQuery(id+"F0.imprint","IMPRINT",FACE,{"disambiguationData":[TD([[makeQuery(id+"F0.imprint","IMPRINT",EDGE,{"derivedFrom":subQ0}),-1.0]])]});}
            extrude(context, id + "F3", {"entities" : qUnion([Q0, Q1, Q2, Q3, Q4, Q5, Q6, Q7, Q8, Q9, Q10, Q11, Q12, Q13, Q14, Q15]), "operationType" : NewBodyOperationType.ADD, "depth" : 4.83 * mm});
        }
        {
            var Q0;
            {var subQ0=sQuery(id+"F0.wireOp",EDGE,"E53");Q0=makeQuery(id+"F0.imprint","IMPRINT",FACE,{"disambiguationData":[TD([[makeQuery(id+"F0.imprint","IMPRINT",EDGE,{"derivedFrom":subQ0}),1.0]])]});}
            var Q1;
            {var subQ4=sQuery(id+"F0.wireOp",EDGE,"E12");Q1=makeQuery(id+"F0.imprint","IMPRINT",FACE,{"disambiguationData":[TD([[makeQuery(id+"F0.imprint","IMPRINT",EDGE,{"derivedFrom":subQ4}),-1.0]])]});}
            var Q2;
            {var subQ4=sQuery(id+"F0.wireOp",EDGE,"E130");Q2=makeQuery(id+"F0.imprint","IMPRINT",FACE,{"disambiguationData":[TD([[makeQuery(id+"F0.imprint","IMPRINT",EDGE,{"derivedFrom":subQ4}),1.0]])]});}
            var Q3;
            {var subQ4=sQuery(id+"F0.wireOp",EDGE,"E55");Q3=makeQuery(id+"F0.imprint","IMPRINT",FACE,{"disambiguationData":[TD([[makeQuery(id+"F0.imprint","IMPRINT",EDGE,{"derivedFrom":subQ4}),1.0]])]});}
            var Q4;
            {var subQ7=sQuery(id+"F0.wireOp",EDGE,"E57");Q4=makeQuery(id+"F0.imprint","IMPRINT",FACE,{"disambiguationData":[TD([[makeQuery(id+"F0.imprint","IMPRINT",EDGE,{"derivedFrom":subQ7}),1.0]])]});}
            var Q5;
            {var subQ4=sQuery(id+"F0.wireOp",EDGE,"E59");Q5=makeQuery(id+"F0.imprint","IMPRINT",FACE,{"disambiguationData":[TD([[makeQuery(id+"F0.imprint","IMPRINT",EDGE,{"derivedFrom":subQ4}),1.0]])]});}
            var Q6;
            {var subQ1=sQuery(id+"F0.wireOp",EDGE,"E115.MirrorCS");Q6=makeQuery(id+"F0.imprint","IMPRINT",FACE,{"disambiguationData":[TD([[makeQuery(id+"F0.imprint","IMPRINT",EDGE,{"derivedFrom":subQ1}),1.0]])]});}
            var Q7;
            {var subQ1=sQuery(id+"F0.wireOp",EDGE,"E109.MirrorCS");Q7=makeQuery(id+"F0.imprint","IMPRINT",FACE,{"disambiguationData":[TD([[makeQuery(id+"F0.imprint","IMPRINT",EDGE,{"derivedFrom":subQ1}),-1.0]])]});}
            var Q8;
            {var subQ1=sQuery(id+"F0.wireOp",EDGE,"E103.MirrorCS");Q8=makeQuery(id+"F0.imprint","IMPRINT",FACE,{"disambiguationData":[TD([[makeQuery(id+"F0.imprint","IMPRINT",EDGE,{"derivedFrom":subQ1}),-1.0]])]});}
            var Q9;
            {var subQ3=sQuery(id+"F0.wireOp",EDGE,"E134.MirrorCS");Q9=makeQuery(id+"F0.imprint","IMPRINT",FACE,{"disambiguationData":[TD([[makeQuery(id+"F0.imprint","IMPRINT",EDGE,{"derivedFrom":subQ3}),-1.0]])]});}
            var Q10;
            {var subQ1=sQuery(id+"F0.wireOp",EDGE,"E85.MirrorCS");Q10=makeQuery(id+"F0.imprint","IMPRINT",FACE,{"disambiguationData":[TD([[makeQuery(id+"F0.imprint","IMPRINT",EDGE,{"derivedFrom":subQ1}),1.0]])]});}
            var Q11;
            {var subQ1=sQuery(id+"F0.wireOp",EDGE,"E72.MirrorCS");Q11=makeQuery(id+"F0.imprint","IMPRINT",FACE,{"disambiguationData":[TD([[makeQuery(id+"F0.imprint","IMPRINT",EDGE,{"derivedFrom":subQ1}),-1.0]])]});}
            extrude(context, id + "F4", {"entities" : qUnion([Q0, Q1, Q2, Q3, Q4, Q5, Q6, Q7, Q8, Q9, Q10, Q11]), "operationType" : NewBodyOperationType.ADD, "depth" : 3.8 * mm});
        }
        {
            var Q0;
            {var subQ3=sQuery(id+"F0.wireOp",EDGE,"E127");Q0=makeQuery(id+"F0.imprint","IMPRINT",FACE,{"disambiguationData":[TD([[makeQuery(id+"F0.imprint","IMPRINT",EDGE,{"derivedFrom":subQ3}),1.0]])]});}
            extrude(context, id + "F5", {"entities" : qUnion([Q0]), "operationType" : NewBodyOperationType.ADD, "depth" : 3.17 * mm});
        }
    });
